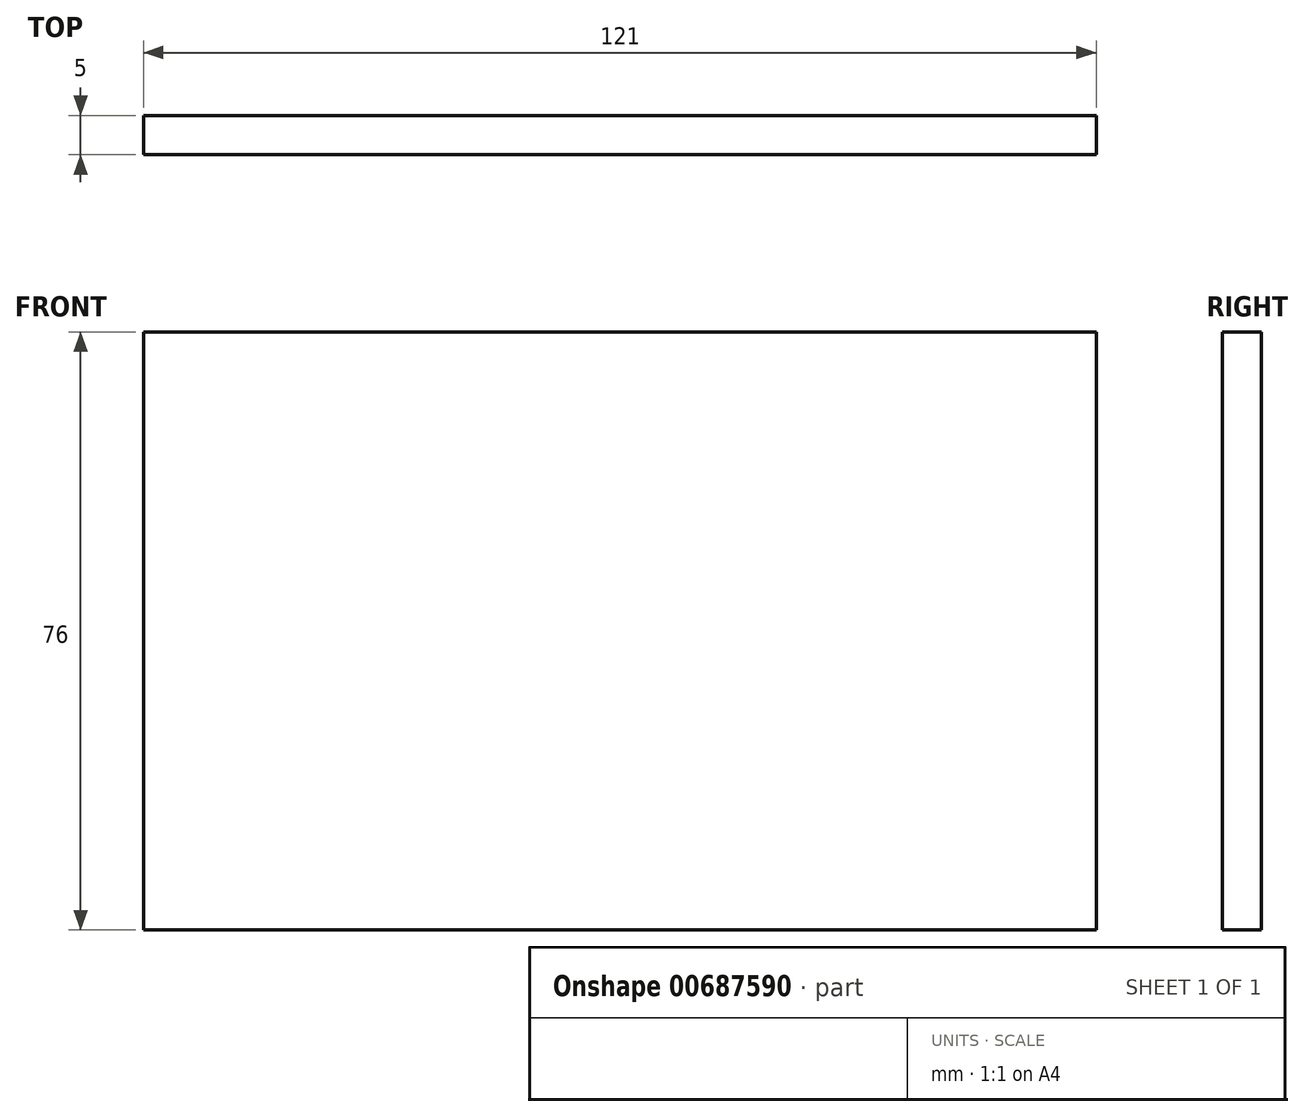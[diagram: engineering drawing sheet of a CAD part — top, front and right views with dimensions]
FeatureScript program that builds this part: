
annotation { "Feature Type Name" : "Feature", "Feature Type Description" : "" }
export const myFeature = defineFeature(function(context is Context, id is Id, definition is map)
    precondition{}
    {
        {
            var Q0;
            Q0=qCreatedBy(makeId("Front.planeOp"),FACE);
            var sketch = newSketch(context, id + "F0", { "sketchPlane" : qUnion([Q0])});
            skLineSegment(sketch, "E0.bottom", {"start": v(-60.5, 38) * mm, "end": v(60.5, 38) * mm});
            skLineSegment(sketch, "E0.top", {"start": v(-60.5, -38) * mm, "end": v(60.5, -38) * mm});
            skLineSegment(sketch, "E0.left", {"start": v(-60.5, 38) * mm, "end": v(-60.5, -38) * mm});
            skLineSegment(sketch, "E0.right", {"start": v(60.5, 38) * mm, "end": v(60.5, -38) * mm});
            skSolve(sketch);
        }
        {
            var Q0;
            Q0=qSketchRegion(id+"F0",true);
            extrude(context, id + "F1", {"entities" : qUnion([Q0]), "depth" : 5 * mm, "offsetDistance" : 25 * mm});
        }
    });
